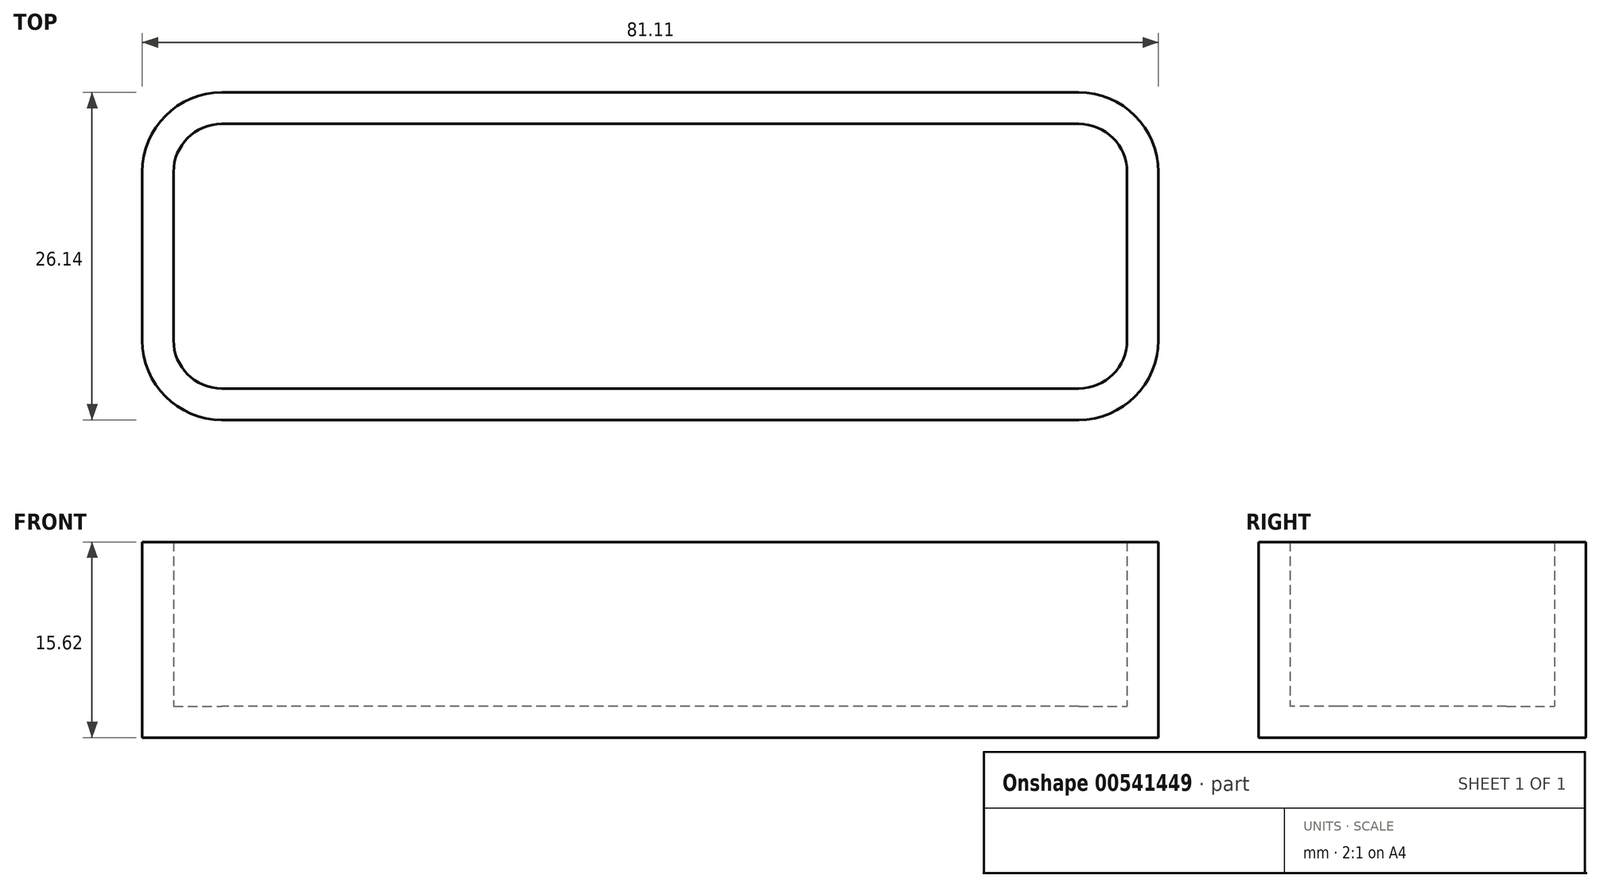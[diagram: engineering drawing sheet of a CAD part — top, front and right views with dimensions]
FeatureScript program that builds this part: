
annotation { "Feature Type Name" : "Feature", "Feature Type Description" : "" }
export const myFeature = defineFeature(function(context is Context, id is Id, definition is map)
    precondition{}
    {
        {
            var Q0;
            Q0=qCreatedBy(makeId("Top.planeOp"),FACE);
            var sketch = newSketch(context, id + "F0", { "sketchPlane" : qUnion([Q0])});
            skLineSegment(sketch, "E0.bottom", {"start": v(31, 26.14) * mm, "end": v(-37.42, 26.14) * mm});
            skLineSegment(sketch, "E0.top", {"start": v(31, 0) * mm, "end": v(-37.42, 0) * mm});
            skLineSegment(sketch, "E0.left", {"start": v(37.34, 19.79) * mm, "end": v(37.34, 6.35) * mm});
            skLineSegment(sketch, "E0.right", {"start": v(-43.77, 19.79) * mm, "end": v(-43.77, 6.35) * mm});
            skPoint(sketch, "E1.visualSharp", {"position": v(-43.77, 26.14) * mm});
            skArc(sketch, "E1.filletArc", {"start": v(-37.42, 26.14) * mm, "mid": v(-41.91, 24.28) * mm, "end": v(-43.77, 19.79) * mm});
            skPoint(sketch, "E2.visualSharp", {"position": v(-43.77, 0) * mm});
            skArc(sketch, "E2.filletArc", {"start": v(-43.77, 6.35) * mm, "mid": v(-41.91, 1.86) * mm, "end": v(-37.42, 0) * mm});
            skPoint(sketch, "E3.visualSharp", {"position": v(37.34, 0) * mm});
            skArc(sketch, "E3.filletArc", {"start": v(31, 0) * mm, "mid": v(35.48, 1.86) * mm, "end": v(37.34, 6.35) * mm});
            skPoint(sketch, "E4.visualSharp", {"position": v(37.34, 26.14) * mm});
            skArc(sketch, "E4.filletArc", {"start": v(37.34, 19.79) * mm, "mid": v(35.48, 24.28) * mm, "end": v(31, 26.14) * mm});
            skSolve(sketch);
        }
        {
            var Q0;
            Q0=makeQuery(id+"F0.imprint","IMPRINT",FACE,{"disambiguationData":[TD([[makeQuery(id+"F0.imprint","IMPRINT",EDGE,{"derivedFrom":sQuery(id+"F0.wireOp",EDGE,"E0.bottom")}),1.0]])]});
            extrude(context, id + "F1", {"entities" : qUnion([Q0]), "depth" : 15.62 * mm, "offsetDistance" : 25 * mm});
        }
        {
            var Q0;
            Q0=makeQuery(id+"F1.opExtrude","CAP_FACE",FACE,{"disambiguationData":[OSD([sQuery(id+"F0.wireOp",EDGE,"E0.bottom"),sQuery(id+"F0.wireOp",EDGE,"E0.top"),sQuery(id+"F0.wireOp",EDGE,"E0.left"),sQuery(id+"F0.wireOp",EDGE,"E0.right"),sQuery(id+"F0.wireOp",EDGE,"E1.filletArc"),sQuery(id+"F0.wireOp",EDGE,"E2.filletArc"),sQuery(id+"F0.wireOp",EDGE,"E3.filletArc"),sQuery(id+"F0.wireOp",EDGE,"E4.filletArc")])],"isStart":false});
            shell(context, id + "F2", {"entities" : qUnion([Q0]), "thickness" : 2.5 * mm});
        }
    });
